# Revit family: FTZC-LR-LG-1-U-WW
name_source: partatom
category: Lighting Fixtures
units: mm (PartAtom-declared; Revit-internal decimal feet)

## family parameters
Cut with Voids When Loaded = No
Host = Face
Light Source = No
Maintain Annotation Orientation = No
Part Type = Normal
Room Calculation Point = No
Round Connector Dimension = Use Diameter
Shared = No

## types (2) — shared parameters
BODY MATERIAL = BODY MATERIAL
Default Elevation = 4' - 0"
Lamp = LED
Manufacturer = BEGHELLI
Wattage Comments = 2 W

## per-type parameters (varying)
| type | Description | LETTER MATERIAL | Model | Type Comments | Type Image |
| FTZC-LR-1-U-WW | The FORTEZZA™ series is constructed from .420” thick, heavy
duty cast aluminum. The faceplates are protected by high abuse
clear polycarbonate, which is recessed into the housing. Tamper
resistant screws are standard. The FORTEZZA™ series comes
standard black although colour options are available upon request.
Single or double versions must be specified. The self-powered
version comes standard with an external LED status indicator and
test switch. | LETTER MATERIAL RED | FTZ-HT-LG-U-U-WW | The Fortezza™ series vandal resistant exit sign is designed to stand up to high abuse areas such as correctional facilities, schools, apartment complexes, and public areas that may be subject to vandalism. | <None> |
| FTZC-LG-1-U-WW | The FORTEZZA™ COMBO has a 120/277VAC input. The 
maintenance free, sealed nickel-cadmium batteries provide a 
minimum 90 minutes of emergency duration. A two stage 
charger and transfer system is standard. Stage 1: a cyclic 
charge which brings the battery voltage to a higher pre-set level 
than its normal float voltage. Stage 2: charger will keep a constant 
charging current. | LETTERS MATERIAL GREEN | FTZC-LG-1-U-WW | The FORTEZZA COMBO is 
designed to stand up to high 
abuse areas such as 
correctional facilities, schools, 
apartment complexes, and 
public areas that may be 
subject to vandalism. | FTZ-C IMAGE.png |

## geometry (parser evidence)
native form markers: Sweep x21
no freeform markers — native parametric forms only
